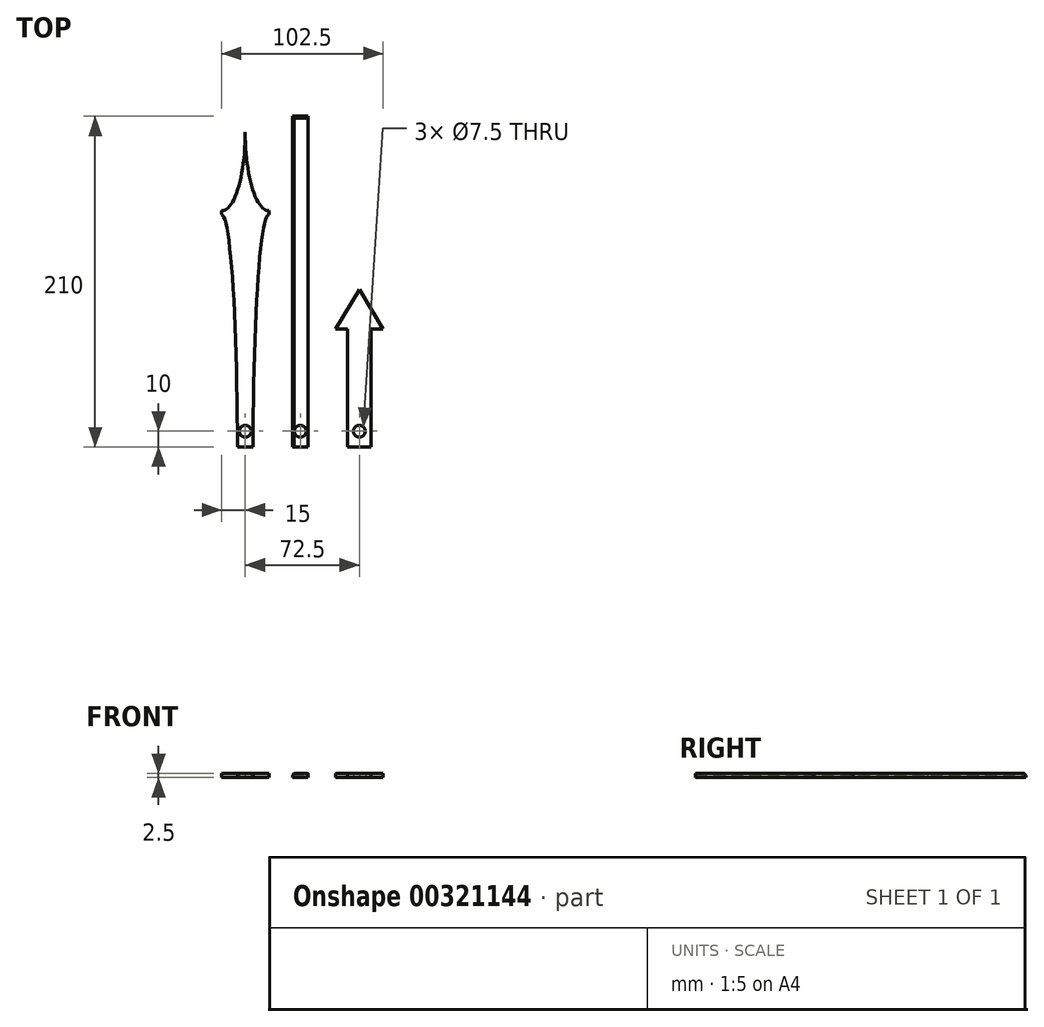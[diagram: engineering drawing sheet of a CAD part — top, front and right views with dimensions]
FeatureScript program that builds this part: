
annotation { "Feature Type Name" : "Feature", "Feature Type Description" : "" }
export const myFeature = defineFeature(function(context is Context, id is Id, definition is map)
    precondition{}
    {
        {
            var Q0;
            Q0=qCreatedBy(makeId("Top.planeOp"),FACE);
            var sketch = newSketch(context, id + "F0", { "sketchPlane" : qUnion([Q0])});
            skLineSegment(sketch, "E0", {"start": v(0, 0) * mm, "end": v(0, 150) * mm});
            skLineSegment(sketch, "E1", {"start": v(0, 150) * mm, "end": v(15, 150) * mm});
            skLineSegment(sketch, "E2", {"start": v(0, 150) * mm, "end": v(0, 200) * mm});
            skLineSegment(sketch, "E3", {"start": v(0, 0) * mm, "end": v(5, 0) * mm});
            skLineSegment(sketch, "E4", {"start": v(5, 0) * mm, "end": v(5, 75) * mm});
            skLineSegment(sketch, "E5.0", {"start": v(5, 147.5) * mm, "end": v(15, 147.5) * mm});
            skEllipticalArc(sketch, "E6", {});
            skLineSegment(sketch, "E7", {"start": v(15, 147.5) * mm, "end": v(15, 150) * mm});
            skEllipticalArc(sketch, "E8", {});
            skPoint(sketch, "E9.orphan", {"position": v(5, 200) * mm});
            skPoint(sketch, "E10.orphan", {"position": v(0, 147.5) * mm});
            skLineSegment(sketch, "E11.trimOffspring", {"start": v(5, 147.5) * mm, "end": v(5, 150) * mm});
            skEllipticalArc(sketch, "E12.MirrorCS", {});
            skEllipticalArc(sketch, "E13.MirrorCS", {});
            skLineSegment(sketch, "E14.MirrorCS", {"start": v(-15, 147.5) * mm, "end": v(-15, 150) * mm});
            skLineSegment(sketch, "E15.MirrorCS", {"start": v(0, 0) * mm, "end": v(-5, 0) * mm});
            skCircle(sketch, "E16", {"center": v(0, 10) * mm, "radius": 3.75 * mm});
            const initialGuessF0  = {"E6": [0.015, 0, 0, -1, 0.1475, 0.01, 3.141592653589793, 4.71238898038469], "E8": [0.015, 0.2, -1, 0, 0.015, 0.05, 6.283185307179586, 1.5707963267948966], "E12.MirrorCS": [-0.015, 0.2, 1, 0, 0.015, 0.05, 4.71238898038469, 6.283185307179586], "E13.MirrorCS": [-0.015, 0, 0, -1, 0.1475, 0.01, 1.5707963267948966, 3.141592653589793]};
            skSetInitialGuess(sketch, initialGuessF0);
            skSolve(sketch);
        }
        {
            var Q0;
            {var subQ0=sQuery(id+"F0.wireOp",EDGE,"E3");Q0=makeQuery(id+"F0.imprint","IMPRINT",FACE,{"disambiguationData":[TD([[makeQuery(id+"F0.imprint","IMPRINT",EDGE,{"derivedFrom":subQ0}),1.0]])]});}
            var Q1;
            Q1=makeQuery(id+"F0.imprint","IMPRINT",FACE,{"disambiguationData":[TD([[makeQuery(id+"F0.imprint","IMPRINT",EDGE,{"derivedFrom":sQuery(id+"F0.wireOp",EDGE,"E5.0")}),1.0]])]});
            var Q2;
            {var subQ0=sQuery(id+"F0.wireOp",EDGE,"E2");Q2=makeQuery(id+"F0.imprint","IMPRINT",FACE,{"disambiguationData":[TD([[makeQuery(id+"F0.imprint","IMPRINT",EDGE,{"derivedFrom":subQ0}),-1.0]])]});}
            var Q3;
            {var subQ0=sQuery(id+"F0.wireOp",EDGE,"E2");Q3=makeQuery(id+"F0.imprint","IMPRINT",FACE,{"disambiguationData":[TD([[makeQuery(id+"F0.imprint","IMPRINT",EDGE,{"derivedFrom":subQ0}),1.0]])]});}
            extrude(context, id + "F1", {"entities" : qUnion([Q0, Q1, Q2, Q3]), "depth" : 2.5 * mm});
        }
        {
            var Q0;
            Q0=qCreatedBy(makeId("Top.planeOp"),FACE);
            var sketch = newSketch(context, id + "F2", { "sketchPlane" : qUnion([Q0])});
            skLineSegment(sketch, "E17", {"start": v(30, 0) * mm, "end": v(40, 0) * mm});
            skLineSegment(sketch, "E18", {"start": v(40, 0) * mm, "end": v(40, 210) * mm});
            skLineSegment(sketch, "E19", {"start": v(30, 0) * mm, "end": v(30, 210) * mm});
            skLineSegment(sketch, "E20", {"start": v(30, 210) * mm, "end": v(40, 210) * mm});
            skLineSegment(sketch, "E21", {"start": v(0, 0) * mm, "end": v(30, 0) * mm});
            skCircle(sketch, "E22", {"center": v(35, 10) * mm, "radius": 3.75 * mm});
            skLineSegment(sketch, "E23", {"start": v(35, 0) * mm, "end": v(35, 10) * mm, "construction": true});
            skSolve(sketch);
        }
        {
            var Q0;
            Q0=qSketchRegion(id+"F2",true);
            extrude(context, id + "F3", {"entities" : qUnion([Q0]), "depth" : 2.5 * mm});
        }
        {
            var Q0;
            Q0=qCreatedBy(makeId("Top.planeOp"),FACE);
            var sketch = newSketch(context, id + "F4", { "sketchPlane" : qUnion([Q0])});
            skLineSegment(sketch, "E24", {"start": v(65, 0) * mm, "end": v(80, 0) * mm});
            skLineSegment(sketch, "E25", {"start": v(65, 0) * mm, "end": v(65, 75) * mm});
            skLineSegment(sketch, "E26", {"start": v(65, 75) * mm, "end": v(57.5, 75) * mm});
            skLineSegment(sketch, "E27", {"start": v(57.5, 75) * mm, "end": v(72.5, 100) * mm});
            skLineSegment(sketch, "E28", {"start": v(72.5, 100) * mm, "end": v(72.5, 0) * mm, "construction": true});
            skPoint(sketch, "E28.endSnap0", {"position": v(72.5, 0) * mm});
            skLineSegment(sketch, "E29", {"start": v(0, 0) * mm, "end": v(65, 0) * mm});
            skLineSegment(sketch, "E30.MirrorCS", {"start": v(80, 0) * mm, "end": v(80, 75) * mm});
            skLineSegment(sketch, "E31.MirrorCS", {"start": v(87.5, 75) * mm, "end": v(72.5, 100) * mm});
            skLineSegment(sketch, "E32.MirrorCS", {"start": v(80, 75) * mm, "end": v(87.5, 75) * mm});
            skCircle(sketch, "E33", {"center": v(72.5, 10) * mm, "radius": 3.75 * mm});
            skSolve(sketch);
        }
        {
            var Q0;
            Q0=qSketchRegion(id+"F4",true);
            extrude(context, id + "F5", {"entities" : qUnion([Q0]), "depth" : 2.5 * mm});
        }
        {
            var Q0;
            Q0=makeQuery(id+"F3.opExtrude","CAP_EDGE",EDGE,{"disambiguationData":[OSD([sQuery(id+"F2.wireOp",EDGE,"E20")])],"isStart":false});
            var Q1;
            Q1=makeQuery(id+"F3.opExtrude","CAP_EDGE",EDGE,{"disambiguationData":[OSD([sQuery(id+"F2.wireOp",EDGE,"E19")])],"isStart":false});
            chamfer(context, id + "F6", {"entities" : qUnion([Q0, Q1]), "width" : 1 * mm, "tangentPropagation" : true});
        }
        {
            var Q0;
            Q0=makeQuery(id+"F3.opExtrude","CAP_EDGE",EDGE,{"disambiguationData":[OSD([sQuery(id+"F2.wireOp",EDGE,"E18")])],"isStart":false});
            var Q1;
            {var subQ0=sQuery(id+"F2.wireOp",EDGE,"E20");Q1=makeQuery(id+"F6.opChamfer","BLEND_EDGE",EDGE,{"blendedFrom":[makeQuery(id+"F3.opExtrude","CAP_EDGE",EDGE,{"disambiguationData":[OSD([subQ0])],"isStart":false}),makeQuery(id+"F3.opExtrude","CAP_FACE",FACE,{"disambiguationData":[OSD([sQuery(id+"F2.wireOp",EDGE,"E17"),sQuery(id+"F2.wireOp",EDGE,"E18"),sQuery(id+"F2.wireOp",EDGE,"E19"),subQ0,sQuery(id+"F2.wireOp",EDGE,"E22")])],"isStart":false})],"blendedInto":[makeQuery(id+"F3.opExtrude","CAP_FACE",FACE,{"disambiguationData":[OSD([sQuery(id+"F2.wireOp",EDGE,"E17"),sQuery(id+"F2.wireOp",EDGE,"E18"),sQuery(id+"F2.wireOp",EDGE,"E19"),subQ0,sQuery(id+"F2.wireOp",EDGE,"E22")])],"isStart":false})]});}
            fillet(context, id + "F7", {"entities" : qUnion([Q0, Q1]), "radius" : 0.4 * mm, "tangentPropagation" : true, "rho" : 0.5, "crossSection" : FilletCrossSection.CONIC, "allowEdgeOverflow" : false});
        }
    });
